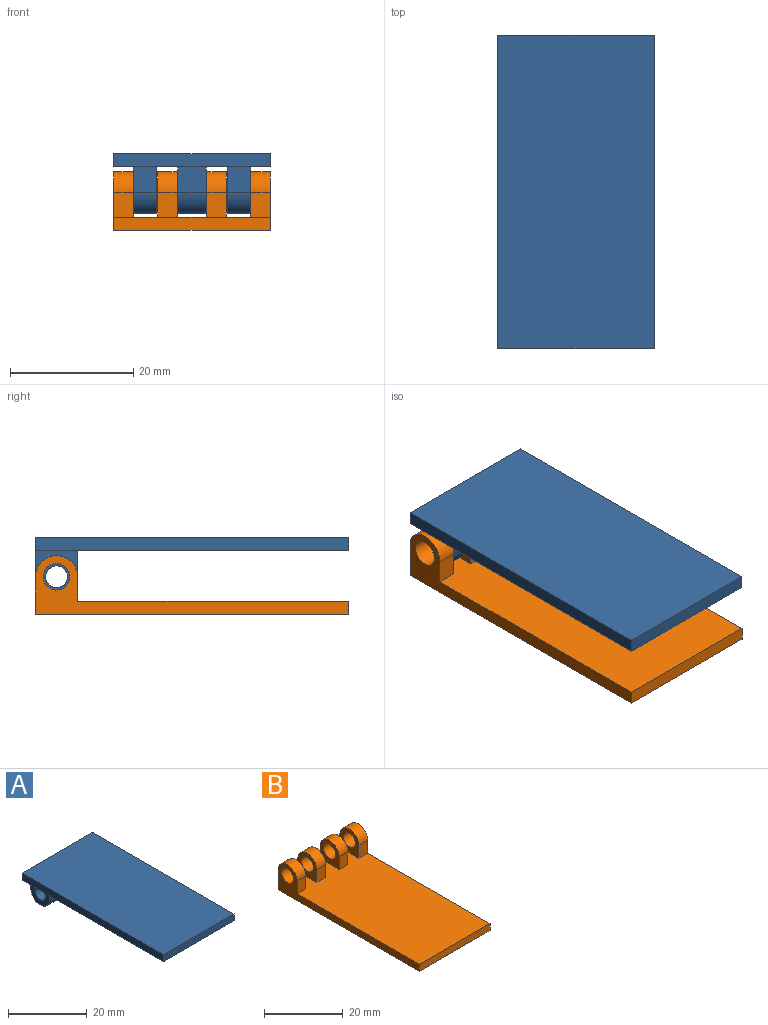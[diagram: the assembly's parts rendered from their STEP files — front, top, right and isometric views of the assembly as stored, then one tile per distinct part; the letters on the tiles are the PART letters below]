
ASSEMBLY  parts=2 mates=1
PART A: 21 faces, bbox 25.4x50.8x9.8 mm
  f0: plane 50.8x25.4mm, normal (0,0,-1), area 1206.7mm2, adj f1,f3,f4,f5,f6,f9,f10,f11
  f1: plane 25.4x6.35mm, normal (0,1,0), area 105.9mm2, adj f0,f2,f4,f5,f7,f9,f10,f12
  f2: plane 50.8x25.4mm, normal (0,0,1), area 1290.3mm2, adj f1,f3,f4,f5
  f3: plane 25.4x2.16mm, normal (0,-1,0), area 54.8mm2, adj f0,f2,f4,f5
  f4: plane 50.8x2.16mm, normal (1,0,0), area 109.7mm2, adj f0,f1,f2,f3
  f5: plane 50.8x2.16mm, normal (-1,0,0), area 109.7mm2, adj f0,f1,f2,f3
  f6: plane 4.57x4.19mm, normal (0,-1,0), area 19.2mm2, adj f0,f7,f9,f10
  f7: cylinder r=3.43mm len=6.86mm, axis (-1,0,0), area 49.3mm2, adj f1,f6,f9,f10
  f8: cylinder r=1.78mm len=4.57mm, axis (-1,0,0), area 51.1mm2, adj f9,f10
  f9: plane 7.62x6.86mm, normal (1,0,0), area 37.3mm2, adj f0,f1,f6,f7,f8
  f10: plane 7.62x6.86mm, normal (-1,0,0), area 37.3mm2, adj f0,f1,f6,f7,f8
  f11: plane 4.19x3.81mm, normal (0,-1,0), area 16mm2, adj f0,f12,f14,f15
  f12: cylinder r=3.43mm len=6.86mm, axis (1,0,0), area 41mm2, adj f1,f11,f14,f15
  f13: cylinder r=1.78mm len=3.81mm, axis (1,0,0), area 42.6mm2, adj f14,f15
  f14: plane 7.62x6.86mm, normal (-1,0,0), area 37.3mm2, adj f0,f1,f11,f12,f13
  f15: plane 7.62x6.86mm, normal (1,0,0), area 37.3mm2, adj f0,f1,f11,f12,f13
  f16: cylinder r=3.43mm len=6.86mm, axis (-1,0,0), area 41mm2, adj f1,f17,f19,f20
  f17: plane 4.19x3.81mm, normal (0,-1,0), area 16mm2, adj f0,f16,f19,f20
  f18: cylinder r=1.78mm len=3.81mm, axis (-1,0,0), area 42.6mm2, adj f19,f20
  f19: plane 7.62x6.86mm, normal (1,0,0), area 37.3mm2, adj f0,f1,f16,f17,f18
  f20: plane 7.62x6.86mm, normal (-1,0,0), area 37.3mm2, adj f0,f1,f16,f17,f18
PART B: 24 faces, bbox 25.4x50.8x9.5 mm
  f0: plane 50.8x25.4mm, normal (0,0,1), area 1203.2mm2, adj f2,f3,f4,f5,f7,f9,f11,f13
  f1: plane 50.8x25.4mm, normal (0,0,-1), area 1290.3mm2, adj f2,f3,f4,f5
  f2: plane 25.4x6.1mm, normal (0,1,0), area 104.8mm2, adj f0,f1,f4,f5,f6,f9,f10,f13
  f3: plane 25.4x2.16mm, normal (0,-1,0), area 54.8mm2, adj f0,f1,f4,f5
  f4: plane 50.8x9.53mm, normal (1,0,0), area 140.5mm2, adj f0,f1,f2,f3,f10,f11,f12
  f5: plane 50.8x9.53mm, normal (-1,0,0), area 140.5mm2, adj f0,f1,f2,f3,f6,f7,f8
  f6: cylinder r=3.43mm len=6.86mm, axis (-1,0,0), area 34.2mm2, adj f2,f5,f7,f9
  f7: plane 3.94x3.18mm, normal (0,-1,0), area 12.5mm2, adj f0,f5,f6,f9
  f8: cylinder r=2.16mm len=4.32mm, axis (-1,0,0), area 43.1mm2, adj f5,f9
  f9: plane 7.37x6.86mm, normal (1,0,0), area 30.8mm2, adj f0,f2,f6,f7,f8
  f10: cylinder r=3.43mm len=6.86mm, axis (1,0,0), area 34.2mm2, adj f2,f4,f11,f13
  f11: plane 3.94x3.18mm, normal (0,-1,0), area 12.5mm2, adj f0,f4,f10,f13
  f12: cylinder r=2.16mm len=4.32mm, axis (1,0,0), area 43.1mm2, adj f4,f13
  f13: plane 7.37x6.86mm, normal (-1,0,0), area 30.8mm2, adj f0,f2,f10,f11,f12
  f14: plane 3.94x3.18mm, normal (0,-1,0), area 12.5mm2, adj f0,f16,f17,f18
  f15: cylinder r=2.16mm len=4.32mm, axis (-1,0,0), area 43.1mm2, adj f17,f18
  f16: cylinder r=3.43mm len=6.86mm, axis (-1,0,0), area 34.2mm2, adj f2,f14,f17,f18
  f17: plane 7.37x6.86mm, normal (1,0,0), area 30.8mm2, adj f0,f2,f14,f15,f16
  f18: plane 7.37x6.86mm, normal (-1,0,0), area 30.8mm2, adj f0,f2,f14,f15,f16
  f19: cylinder r=3.43mm len=6.86mm, axis (1,0,0), area 34.2mm2, adj f2,f20,f22,f23
  f20: plane 3.94x3.18mm, normal (0,-1,0), area 12.5mm2, adj f0,f19,f22,f23
  f21: cylinder r=2.16mm len=4.32mm, axis (1,0,0), area 43.1mm2, adj f22,f23
  f22: plane 7.37x6.86mm, normal (-1,0,0), area 30.8mm2, adj f0,f2,f19,f20,f21
  f23: plane 7.37x6.86mm, normal (1,0,0), area 30.8mm2, adj f0,f2,f19,f20,f21
PLACE A t=(1.54,-0.06,-14.42)mm
PLACE B t=(-11.16,8.66,-11.33)mm
MATE revolute A.f7 <-> B.f6  axis (1,0,0) through (3.83,16.77,-2.79)mm
